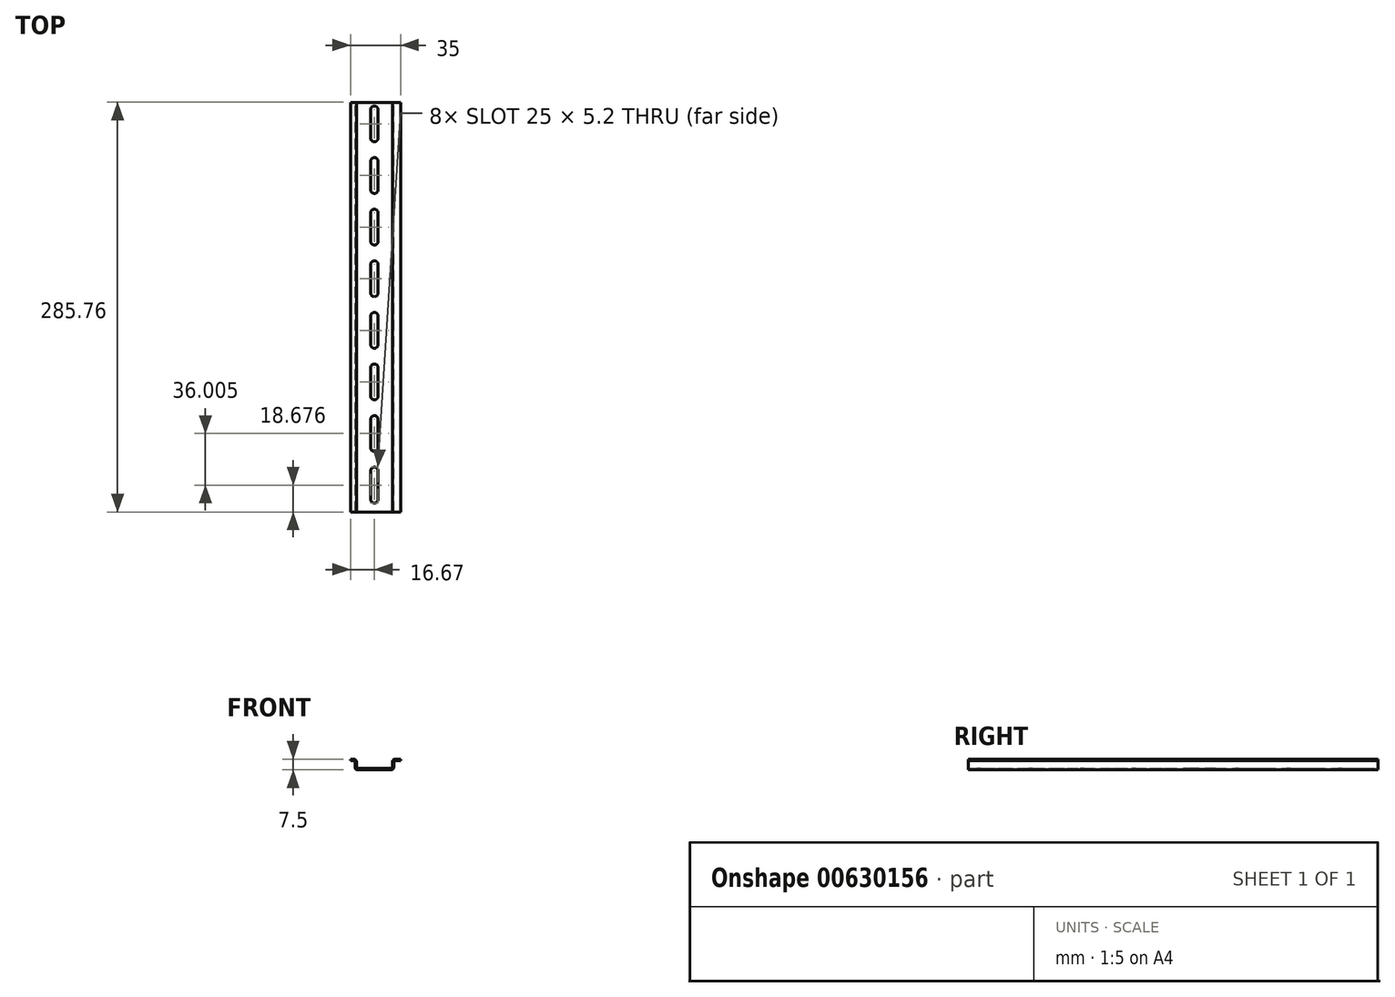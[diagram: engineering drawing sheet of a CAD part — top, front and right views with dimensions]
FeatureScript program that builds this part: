
annotation { "Feature Type Name" : "Feature", "Feature Type Description" : "" }
export const myFeature = defineFeature(function(context is Context, id is Id, definition is map)
    precondition{}
    {
        {
            var Q0;
            Q0=qCreatedBy(makeId("Front.planeOp"),FACE);
            var sketch = newSketch(context, id + "F0", { "sketchPlane" : qUnion([Q0])});
            skLineSegment(sketch, "E0", {"start": v(-11.5, 0) * mm, "end": v(11.5, 0) * mm});
            skLineSegment(sketch, "E1", {"start": v(13.5, 2) * mm, "end": v(13.5, 5.5) * mm});
            skLineSegment(sketch, "E2", {"start": v(14.5, 6.5) * mm, "end": v(18.33, 6.5) * mm});
            skLineSegment(sketch, "E3", {"start": v(18.33, 6.5) * mm, "end": v(18.33, 7.5) * mm});
            skLineSegment(sketch, "E4", {"start": v(18.33, 7.5) * mm, "end": v(14.52, 7.5) * mm});
            skLineSegment(sketch, "E5", {"start": v(12.52, 5.5) * mm, "end": v(12.52, 2) * mm});
            skLineSegment(sketch, "E6", {"start": v(11.52, 1) * mm, "end": v(-11.48, 1) * mm});
            skLineSegment(sketch, "E7", {"start": v(-12.48, 2) * mm, "end": v(-12.48, 5.5) * mm});
            skLineSegment(sketch, "E8", {"start": v(-14.48, 7.5) * mm, "end": v(-16.67, 7.5) * mm});
            skLineSegment(sketch, "E9", {"start": v(-16.67, 7.5) * mm, "end": v(-16.67, 6.5) * mm});
            skLineSegment(sketch, "E10", {"start": v(-16.67, 6.5) * mm, "end": v(-14.5, 6.5) * mm});
            skLineSegment(sketch, "E11", {"start": v(-13.5, 5.5) * mm, "end": v(-13.5, 2) * mm});
            skPoint(sketch, "E12.visualSharp", {"position": v(-12.48, 1) * mm});
            skArc(sketch, "E12.filletArc", {"start": v(-12.48, 2) * mm, "mid": v(-12.2, 1.3) * mm, "end": v(-11.48, 1) * mm});
            skPoint(sketch, "E13.visualSharp", {"position": v(12.52, 1) * mm});
            skArc(sketch, "E13.filletArc", {"start": v(11.52, 1) * mm, "mid": v(12.22, 1.3) * mm, "end": v(12.52, 2) * mm});
            skPoint(sketch, "E14.visualSharp", {"position": v(13.5, 6.5) * mm});
            skArc(sketch, "E14.filletArc", {"start": v(14.5, 6.5) * mm, "mid": v(13.8, 6.2) * mm, "end": v(13.5, 5.5) * mm});
            skPoint(sketch, "E15.visualSharp", {"position": v(-13.5, 6.5) * mm});
            skArc(sketch, "E15.filletArc", {"start": v(-13.5, 5.5) * mm, "mid": v(-13.8, 6.2) * mm, "end": v(-14.5, 6.5) * mm});
            skPoint(sketch, "E16.visualSharp", {"position": v(12.52, 7.5) * mm});
            skArc(sketch, "E16.filletArc", {"start": v(14.52, 7.5) * mm, "mid": v(13.1, 6.92) * mm, "end": v(12.52, 5.5) * mm});
            skPoint(sketch, "E17.visualSharp", {"position": v(13.5, 0) * mm});
            skArc(sketch, "E17.filletArc", {"start": v(11.5, 0) * mm, "mid": v(12.91, 0.59) * mm, "end": v(13.5, 2) * mm});
            skPoint(sketch, "E18.visualSharp", {"position": v(-13.5, 0) * mm});
            skArc(sketch, "E18.filletArc", {"start": v(-13.5, 2) * mm, "mid": v(-12.91, 0.59) * mm, "end": v(-11.5, 0) * mm});
            skPoint(sketch, "E19.visualSharp", {"position": v(-12.48, 7.5) * mm});
            skArc(sketch, "E19.filletArc", {"start": v(-12.48, 5.5) * mm, "mid": v(-13.07, 6.92) * mm, "end": v(-14.48, 7.5) * mm});
            skSolve(sketch);
        }
        {
            var Q0;
            Q0=qSketchRegion(id+"F0",true);
            extrude(context, id + "F1", {"entities" : qUnion([Q0]), "endBound" : BoundingType.SYMMETRIC, "depth" : 285.75 * mm, "offsetDistance" : 25.4 * mm});
        }
        {
            var Q0;
            Q0=makeQuery(id+"F1.opExtrude","SWEPT_FACE",FACE,{"disambiguationData":[OSD([sQuery(id+"F0.wireOp",EDGE,"E6")])]});
            var sketch = newSketch(context, id + "F2", { "sketchPlane" : qUnion([Q0])});
            skLineSegment(sketch, "E20", {"start": v(-2.6, 29.7) * mm, "end": v(-2.6, 9.9) * mm});
            skArc(sketch, "E21", {"start": v(-2.6, 9.9) * mm, "mid": v(0, 7.3) * mm, "end": v(2.6, 9.9) * mm});
            skLineSegment(sketch, "E22", {"start": v(2.6, 9.9) * mm, "end": v(2.6, 29.7) * mm});
            skArc(sketch, "E23", {"start": v(2.6, 29.7) * mm, "mid": v(0, 32.3) * mm, "end": v(-2.6, 29.7) * mm});
            skLineSegment(sketch, "E24", {"start": v(2.6, 45.9) * mm, "end": v(2.6, 65.7) * mm});
            skLineSegment(sketch, "E25", {"start": v(-2.6, 65.7) * mm, "end": v(-2.6, 45.9) * mm});
            skArc(sketch, "E26", {"start": v(2.6, 65.7) * mm, "mid": v(0, 68.3) * mm, "end": v(-2.6, 65.7) * mm});
            skArc(sketch, "E27", {"start": v(-2.6, 45.9) * mm, "mid": v(0, 43.3) * mm, "end": v(2.6, 45.9) * mm});
            skLineSegment(sketch, "E28", {"start": v(2.6, 81.9) * mm, "end": v(2.6, 101.7) * mm});
            skLineSegment(sketch, "E29", {"start": v(-2.6, 101.7) * mm, "end": v(-2.6, 81.9) * mm});
            skArc(sketch, "E30", {"start": v(2.6, 101.7) * mm, "mid": v(0, 104.3) * mm, "end": v(-2.6, 101.7) * mm});
            skArc(sketch, "E31", {"start": v(-2.6, 81.9) * mm, "mid": v(0, 79.3) * mm, "end": v(2.6, 81.9) * mm});
            skLineSegment(sketch, "E32", {"start": v(2.6, 117.9) * mm, "end": v(2.6, 137.7) * mm});
            skLineSegment(sketch, "E33", {"start": v(-2.6, 137.7) * mm, "end": v(-2.6, 117.9) * mm});
            skArc(sketch, "E34", {"start": v(2.6, 137.7) * mm, "mid": v(0, 140.3) * mm, "end": v(-2.6, 137.7) * mm});
            skArc(sketch, "E35", {"start": v(-2.6, 117.9) * mm, "mid": v(0, 115.3) * mm, "end": v(2.6, 117.9) * mm});
            skLineSegment(sketch, "E36", {"start": v(2.6, -26.1) * mm, "end": v(2.6, -6.3) * mm});
            skLineSegment(sketch, "E37", {"start": v(-2.6, -6.3) * mm, "end": v(-2.6, -26.1) * mm});
            skArc(sketch, "E38", {"start": v(2.6, -6.3) * mm, "mid": v(0, -3.7) * mm, "end": v(-2.6, -6.3) * mm});
            skArc(sketch, "E39", {"start": v(-2.6, -26.1) * mm, "mid": v(0, -28.7) * mm, "end": v(2.6, -26.1) * mm});
            skLineSegment(sketch, "E40", {"start": v(2.6, -62.1) * mm, "end": v(2.6, -42.3) * mm});
            skLineSegment(sketch, "E41", {"start": v(-2.6, -42.3) * mm, "end": v(-2.6, -62.1) * mm});
            skArc(sketch, "E42", {"start": v(2.6, -42.3) * mm, "mid": v(0, -39.7) * mm, "end": v(-2.6, -42.3) * mm});
            skArc(sketch, "E43", {"start": v(-2.6, -62.1) * mm, "mid": v(0, -64.7) * mm, "end": v(2.6, -62.1) * mm});
            skLineSegment(sketch, "E44", {"start": v(2.6, -98.1) * mm, "end": v(2.6, -78.3) * mm});
            skLineSegment(sketch, "E45", {"start": v(-2.6, -78.3) * mm, "end": v(-2.6, -98.1) * mm});
            skArc(sketch, "E46", {"start": v(2.6, -78.3) * mm, "mid": v(0, -75.7) * mm, "end": v(-2.6, -78.3) * mm});
            skArc(sketch, "E47", {"start": v(-2.6, -98.1) * mm, "mid": v(0, -100.7) * mm, "end": v(2.6, -98.1) * mm});
            skLineSegment(sketch, "E48", {"start": v(2.6, -134.1) * mm, "end": v(2.6, -114.3) * mm});
            skLineSegment(sketch, "E49", {"start": v(-2.6, -114.3) * mm, "end": v(-2.6, -134.1) * mm});
            skArc(sketch, "E50", {"start": v(2.6, -114.3) * mm, "mid": v(0, -111.7) * mm, "end": v(-2.6, -114.3) * mm});
            skArc(sketch, "E51", {"start": v(-2.6, -134.1) * mm, "mid": v(0, -136.7) * mm, "end": v(2.6, -134.1) * mm});
            skSolve(sketch);
        }
        {
            var Q0;
            Q0=qSketchRegion(id+"F2",true);
            extrude(context, id + "F3", {"entities" : qUnion([Q0]), "operationType" : NewBodyOperationType.REMOVE, "endBound" : BoundingType.THROUGH_ALL, "oppositeDirection" : true, "depth" : 25.4 * mm});
        }
    });
